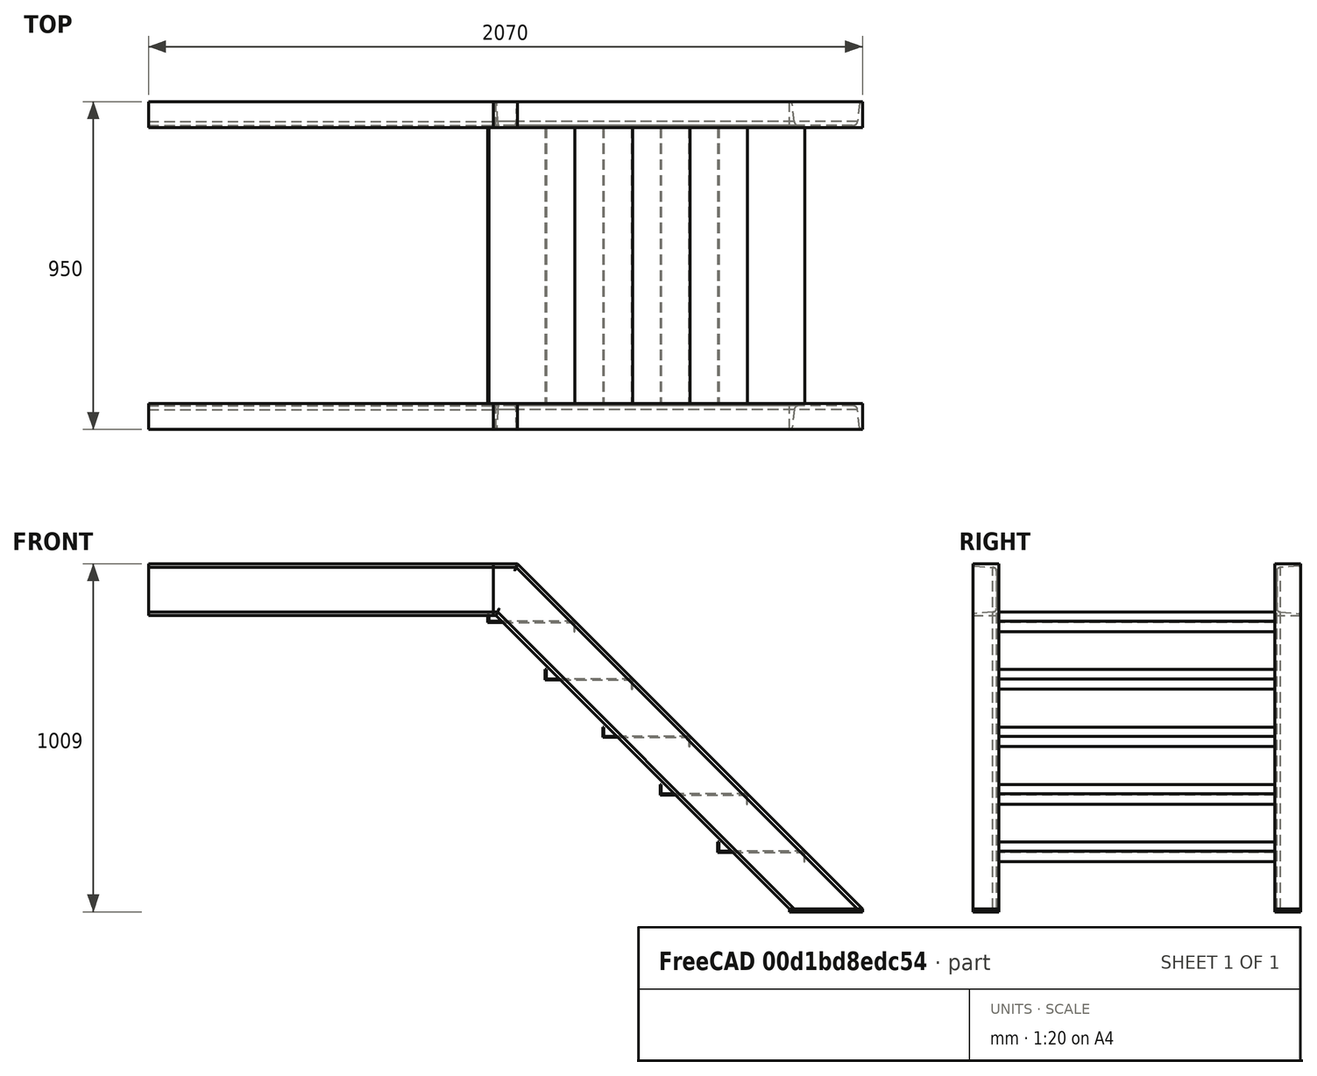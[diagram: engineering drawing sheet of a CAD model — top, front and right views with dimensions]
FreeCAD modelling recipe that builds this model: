
FCSTD DOCUMENT  (FreeCAD 1.0R39109 (Git))
Label: wolkWay
License: All rights reserved
objects: Part::FeaturePython×4, Part::Extrusion×2, Part::Part2DObjectPython×1
note: 7 computed .brp shape members not serialized (recipe doc carries the construction recipe); baked Part::Feature solids carry a one-line shape summary decoded from their .brp

FEATURE [Part::FeaturePython] SteelStair  # WARN: FeaturePython — macro-defined, semantics opaque (R4)
  H = 1000
  HighPlace = false
  L = 1000
  L1 = 70
  Position = 2
  body = 78.6198
  handrail = 0
  mass = 78.6198
  size = 1
  t = 9
  type = 0
  w = 800
FEATURE [Part::FeaturePython] Clone  label="SteelStair001"  # Draft clone (typed FeaturePython)
  AttacherType = Attacher::AttachEngine3D
  Fuse = false
  Objects = -> [SteelStair]
  Placement = pos=(2927.87,-800,0) rot=(0,0,1;3.14159rad)
  Scale = (1,1,1)
FEATURE [Part::Part2DObjectPython] Rectangle  # Draft 2D object (typed FeaturePython)
  Area = 182985
  ChamferSize = 0
  Columns = 1
  FilletRadius = 0
  Height = 177.394
  Length = 1031.51
  MakeFace = true
  Placement = pos=(963.9,-911.121,948.238) rot=(0.57735,0.57735,0.57735;2.0944rad)
  Rows = 1
FEATURE [Part::FeaturePython] ChannelSteel  # WARN: FeaturePython — macro-defined, semantics opaque (R4)
  B = 75
  H = 150
  L = 5500
  Placement = pos=(963.934,-1.137e-13,956.066) rot=(0,0,1;1.5708rad)
  Solid = false
  g0 = 7.85
  mass = 0
  size = 3
  standard = SS
  t1 = 6.5
  t2 = 10
  type = 01_Channel
FEATURE [Part::FeaturePython] Clone001  label="ChannelSteel001"  # Draft clone (typed FeaturePython)
  AttacherType = Attacher::AttachEngine3D
  Fuse = false
  Objects = -> [ChannelSteel]
  Placement = pos=(963.934,-800,956.066) rot=(0,0,1;4.71239rad)
  Scale = (1,1,1)
FEATURE [Part::Extrusion] Extrude
  Base = -> ChannelSteel
  Dir = (-1,-2e-16,0)
  DirMode = 2
  FaceMakerClass = Part::FaceMakerBullseye
  FaceMakerMode = 3
  LengthFwd = 1000
  LengthRev = 0
  Reversed = true
  Solid = false
  Symmetric = false
FEATURE [Part::Extrusion] Extrude001
  Base = -> Clone001
  Dir = (1,-2e-16,0)
  DirMode = 2
  FaceMakerClass = Part::FaceMakerBullseye
  FaceMakerMode = 3
  LengthFwd = 1000
  LengthRev = 0
  Solid = false
  Symmetric = false
